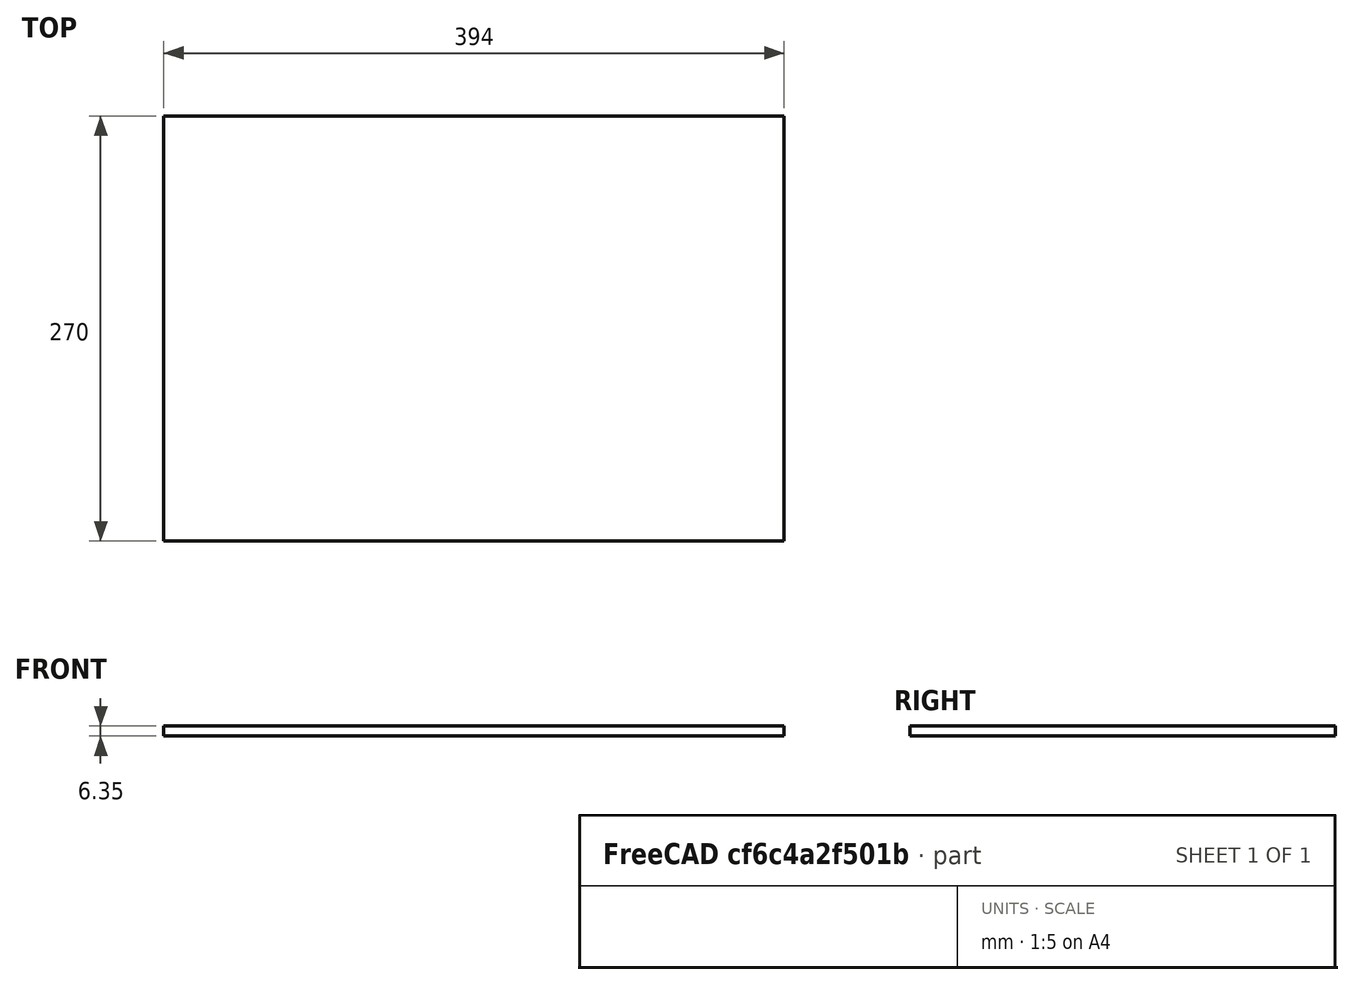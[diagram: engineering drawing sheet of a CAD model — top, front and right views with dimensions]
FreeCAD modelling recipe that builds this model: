
FCSTD DOCUMENT  (FreeCAD 0.20R29177 +426 (Git))
Label: Platform
License: All rights reserved
LicenseURL: http://en.wikipedia.org/wiki/All_rights_reserved
objects: App::DocumentObjectGroup×3, PartDesign::CoordinateSystem×1, App::FeaturePython×1, Sketcher::SketchObject×1, PartDesign::Pad×1, PartDesign::Body×1, App::Part×1
note: 5 computed .brp shape members not serialized (recipe doc carries the construction recipe); baked Part::Feature solids carry a one-line shape summary decoded from their .brp

FEATURE [App::DocumentObjectGroup] Parts
FEATURE [PartDesign::CoordinateSystem] LCS_Origin
  AttacherType = Attacher::AttachEngine3D
  MapMode = 2
  Support = -> [X_Axis]
FEATURE [App::DocumentObjectGroup] Constraints
FEATURE [App::FeaturePython] Variables  # WARN: FeaturePython — macro-defined, semantics opaque (R4)
  Type = App::PropertyContainer
FEATURE [App::DocumentObjectGroup] Configurations
FEATURE [Sketcher::SketchObject] Sketch
  FullyConstrained = true
  MapMode = 5
  Support = -> [XY_Plane001]
  sketch-geometry (5):
    g0: LineSegment StartX=-197 StartY=135 StartZ=0 EndX=-197 EndY=-135 EndZ=0
    g1: LineSegment StartX=-197 StartY=-135 StartZ=0 EndX=197 EndY=-135 EndZ=0
    g2: LineSegment StartX=197 StartY=-135 StartZ=0 EndX=197 EndY=135 EndZ=0
    g3: LineSegment StartX=197 StartY=135 StartZ=0 EndX=-197 EndY=135 EndZ=0
    g4: GeomPoint X=0 Y=0 Z=0
  constraints (12):
    c: Coincident(g0,g1)
    c: Coincident(g1,g2)
    c: Coincident(g2,g3)
    c: Coincident(g3,g0)
    c: Horizontal(g1)
    c: Horizontal(g3)
    c: Vertical(g0)
    c: Vertical(g2)
    c: Symmetric(g1,g0,g4)
    c: Coincident(g4,g-1)
    c: DistanceX(g3,g3) = 394
    c: DistanceY(g2,g2) = 270
FEATURE [PartDesign::Pad] Pad
  Direction = (0,0,1)
  Length = 6.35
  Length2 = 10
  Profile = -> Sketch
  ReferenceAxis = -> Sketch [N_Axis]
  Type = 0
FEATURE [PartDesign::Body] Body
  Group = -> [Sketch,Pad]
  Origin = -> Origin001
  Tip = -> Pad
FEATURE [App::Part] Assembly
  AssemblyType = Part::Link
  Group = -> [LCS_Origin,Constraints,Variables,Configurations,Body]
  Origin = -> Origin
  Type = Assembly
